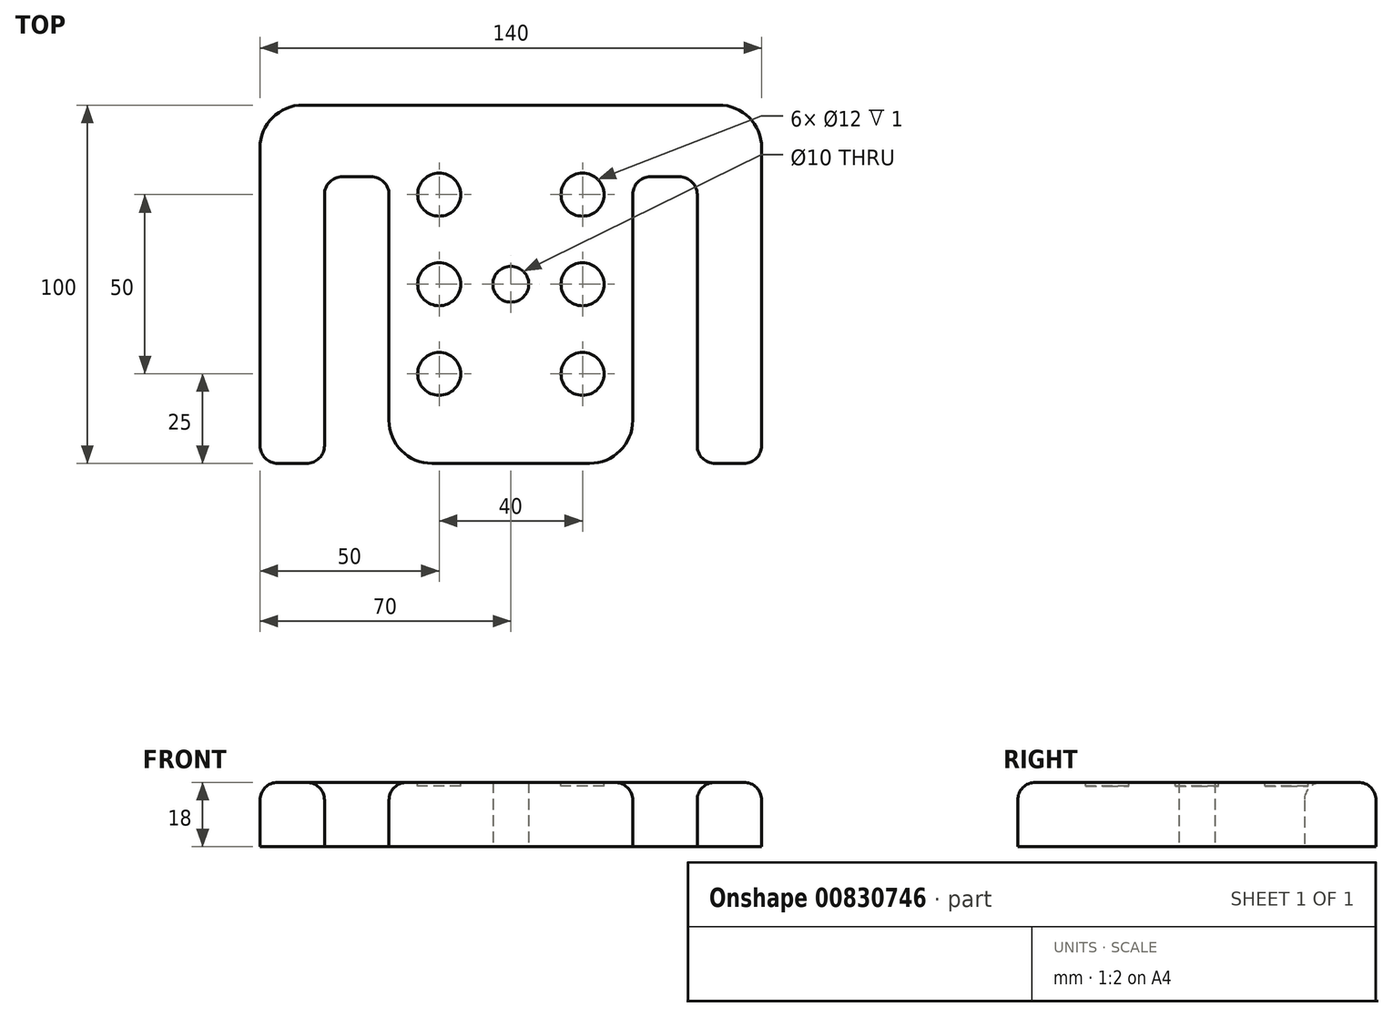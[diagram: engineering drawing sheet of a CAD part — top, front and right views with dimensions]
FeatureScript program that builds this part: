
annotation { "Feature Type Name" : "Feature", "Feature Type Description" : "" }
export const myFeature = defineFeature(function(context is Context, id is Id, definition is map)
    precondition{}
    {
        {
            var Q0;
            Q0=qCreatedBy(makeId("Top.planeOp"),FACE);
            var sketch = newSketch(context, id + "F0", { "sketchPlane" : qUnion([Q0])});
            skLineSegment(sketch, "E0.top", {"start": v(22, -50) * mm, "end": v(0, -50) * mm});
            skPoint(sketch, "E0.middle", {"position": v(0, 0) * mm});
            skLineSegment(sketch, "E1.bottom", {"start": v(65, -50) * mm, "end": v(57, -50) * mm});
            skLineSegment(sketch, "E1.top", {"start": v(58, 50) * mm, "end": v(0, 50) * mm});
            skLineSegment(sketch, "E1.left", {"start": v(70, -45) * mm, "end": v(70, 38) * mm});
            skLineSegment(sketch, "E2.top", {"start": v(47, 30) * mm, "end": v(39, 30) * mm});
            skLineSegment(sketch, "E3", {"start": v(34, -38) * mm, "end": v(34, 25) * mm});
            skLineSegment(sketch, "E4", {"start": v(52, -45) * mm, "end": v(52, 25) * mm});
            skLineSegment(sketch, "E5", {"start": v(0, 50) * mm, "end": v(0, 0) * mm, "construction": true});
            skLineSegment(sketch, "E6", {"start": v(0, -50) * mm, "end": v(0, 0) * mm, "construction": true});
            skLineSegment(sketch, "E7.bottom", {"start": v(80, 65) * mm, "end": v(-80, 65) * mm, "construction": true});
            skLineSegment(sketch, "E7.top", {"start": v(80, -65) * mm, "end": v(-80, -65) * mm, "construction": true});
            skLineSegment(sketch, "E7.left", {"start": v(80, 65) * mm, "end": v(80, -65) * mm, "construction": true});
            skLineSegment(sketch, "E7.right", {"start": v(-80, 65) * mm, "end": v(-80, -65) * mm, "construction": true});
            skLineSegment(sketch, "E8.MirrorCS", {"start": v(-52, -45) * mm, "end": v(-52, 25) * mm});
            skLineSegment(sketch, "E9.MirrorCS", {"start": v(-70, -45) * mm, "end": v(-70, 38) * mm});
            skLineSegment(sketch, "E10.MirrorCS", {"start": v(-47, 30) * mm, "end": v(-39, 30) * mm});
            skLineSegment(sketch, "E11.MirrorCS", {"start": v(-65, -50) * mm, "end": v(-57, -50) * mm});
            skLineSegment(sketch, "E12.MirrorCS", {"start": v(-58, 50) * mm, "end": v(0, 50) * mm});
            skLineSegment(sketch, "E13.MirrorCS", {"start": v(-34, -38) * mm, "end": v(-34, 25) * mm});
            skLineSegment(sketch, "E14.MirrorCS", {"start": v(-22, -50) * mm, "end": v(0, -50) * mm});
            skPoint(sketch, "E15.visualSharp", {"position": v(-52, 30) * mm});
            skArc(sketch, "E15.filletArc", {"start": v(-47, 30) * mm, "mid": v(-50.54, 28.54) * mm, "end": v(-52, 25) * mm});
            skPoint(sketch, "E16.visualSharp", {"position": v(-34, 30) * mm});
            skArc(sketch, "E16.filletArc", {"start": v(-34, 25) * mm, "mid": v(-35.46, 28.54) * mm, "end": v(-39, 30) * mm});
            skPoint(sketch, "E17.visualSharp", {"position": v(34, 30) * mm});
            skArc(sketch, "E17.filletArc", {"start": v(39, 30) * mm, "mid": v(35.46, 28.54) * mm, "end": v(34, 25) * mm});
            skPoint(sketch, "E18.visualSharp", {"position": v(52, 30) * mm});
            skArc(sketch, "E18.filletArc", {"start": v(52, 25) * mm, "mid": v(50.54, 28.54) * mm, "end": v(47, 30) * mm});
            skPoint(sketch, "E19.visualSharp", {"position": v(52, -50) * mm});
            skArc(sketch, "E19.filletArc", {"start": v(52, -45) * mm, "mid": v(53.46, -48.54) * mm, "end": v(57, -50) * mm});
            skPoint(sketch, "E20.visualSharp", {"position": v(34, -50) * mm});
            skArc(sketch, "E20.filletArc", {"start": v(22, -50) * mm, "mid": v(30.49, -46.49) * mm, "end": v(34, -38) * mm});
            skPoint(sketch, "E21.visualSharp", {"position": v(-34, -50) * mm});
            skArc(sketch, "E21.filletArc", {"start": v(-34, -38) * mm, "mid": v(-30.49, -46.49) * mm, "end": v(-22, -50) * mm});
            skPoint(sketch, "E22.visualSharp", {"position": v(-52, -50) * mm});
            skArc(sketch, "E22.filletArc", {"start": v(-57, -50) * mm, "mid": v(-53.46, -48.54) * mm, "end": v(-52, -45) * mm});
            skPoint(sketch, "E23.visualSharp", {"position": v(-70, -50) * mm});
            skArc(sketch, "E23.filletArc", {"start": v(-70, -45) * mm, "mid": v(-68.54, -48.54) * mm, "end": v(-65, -50) * mm});
            skPoint(sketch, "E24.visualSharp", {"position": v(-70, 50) * mm});
            skArc(sketch, "E24.filletArc", {"start": v(-58, 50) * mm, "mid": v(-66.49, 46.49) * mm, "end": v(-70, 38) * mm});
            skPoint(sketch, "E25.visualSharp", {"position": v(70, 50) * mm});
            skArc(sketch, "E25.filletArc", {"start": v(70, 38) * mm, "mid": v(66.49, 46.49) * mm, "end": v(58, 50) * mm});
            skPoint(sketch, "E26.visualSharp", {"position": v(70, -50) * mm});
            skArc(sketch, "E26.filletArc", {"start": v(65, -50) * mm, "mid": v(68.54, -48.54) * mm, "end": v(70, -45) * mm});
            skCircle(sketch, "E27", {"center": v(0, 0) * mm, "radius": 5 * mm});
            skSolve(sketch);
        }
        {
            var Q0;
            Q0=makeQuery(id+"F0.imprint","IMPRINT",FACE,{"disambiguationData":[TD([[makeQuery(id+"F0.imprint","IMPRINT",EDGE,{"derivedFrom":sQuery(id+"F0.wireOp",EDGE,"E0.top")}),-1.0]])]});
            extrude(context, id + "F1", {"entities" : qUnion([Q0]), "depth" : 18 * mm, "offsetDistance" : 25 * mm});
        }
        {
            var Q0;
            Q0=makeQuery(id+"F1.opExtrude","CAP_FACE",FACE,{"disambiguationData":[OSD([sQuery(id+"F0.wireOp",EDGE,"E0.top"),sQuery(id+"F0.wireOp",EDGE,"E1.bottom"),sQuery(id+"F0.wireOp",EDGE,"E1.top"),sQuery(id+"F0.wireOp",EDGE,"E1.left"),sQuery(id+"F0.wireOp",EDGE,"E2.top"),sQuery(id+"F0.wireOp",EDGE,"E3"),sQuery(id+"F0.wireOp",EDGE,"E4"),sQuery(id+"F0.wireOp",EDGE,"E8.MirrorCS"),sQuery(id+"F0.wireOp",EDGE,"E9.MirrorCS"),sQuery(id+"F0.wireOp",EDGE,"E10.MirrorCS"),sQuery(id+"F0.wireOp",EDGE,"E11.MirrorCS"),sQuery(id+"F0.wireOp",EDGE,"E12.MirrorCS"),sQuery(id+"F0.wireOp",EDGE,"E13.MirrorCS"),sQuery(id+"F0.wireOp",EDGE,"E14.MirrorCS"),sQuery(id+"F0.wireOp",EDGE,"E15.filletArc"),sQuery(id+"F0.wireOp",EDGE,"E16.filletArc"),sQuery(id+"F0.wireOp",EDGE,"E17.filletArc"),sQuery(id+"F0.wireOp",EDGE,"E18.filletArc"),sQuery(id+"F0.wireOp",EDGE,"E19.filletArc"),sQuery(id+"F0.wireOp",EDGE,"E20.filletArc"),sQuery(id+"F0.wireOp",EDGE,"E21.filletArc"),sQuery(id+"F0.wireOp",EDGE,"E22.filletArc"),sQuery(id+"F0.wireOp",EDGE,"E23.filletArc"),sQuery(id+"F0.wireOp",EDGE,"E24.filletArc"),sQuery(id+"F0.wireOp",EDGE,"E25.filletArc"),sQuery(id+"F0.wireOp",EDGE,"E26.filletArc")])],"isStart":false});
            var sketch = newSketch(context, id + "F2", { "sketchPlane" : qUnion([Q0])});
            skLineSegment(sketch, "E28", {"start": v(20, -50) * mm, "end": v(20, 50) * mm, "construction": true});
            skCircle(sketch, "E29", {"center": v(20, 0) * mm, "radius": 6 * mm});
            skCircle(sketch, "E30", {"center": v(20, 25) * mm, "radius": 6 * mm});
            skCircle(sketch, "E31", {"center": v(20, -25) * mm, "radius": 6 * mm});
            skCircle(sketch, "E32.MirrorC", {"center": v(-20, 25) * mm, "radius": 6 * mm});
            skCircle(sketch, "E33.MirrorC", {"center": v(-20, 0) * mm, "radius": 6 * mm});
            skCircle(sketch, "E34.MirrorC", {"center": v(-20, -25) * mm, "radius": 6 * mm});
            skSolve(sketch);
        }
        {
            var Q0;
            Q0 = qSketchRegion(id + "F2", true);
            extrude(context, id + "F3", {"entities" : qUnion([Q0]), "operationType" : NewBodyOperationType.REMOVE, "depth" : -1 * mm, "offsetDistance" : 25 * mm});
        }
        {
            var Q0;
            Q0=makeQuery(id+"F1.opExtrude","CAP_EDGE",EDGE,{"disambiguationData":[OSD([sQuery(id+"F0.wireOp",EDGE,"E1.left")])],"isStart":false});
            fillet(context, id + "F4", {"entities" : qUnion([Q0]), "radius" : 5 * mm, "tangentPropagation" : true, "allowEdgeOverflow" : false});
        }
    });
